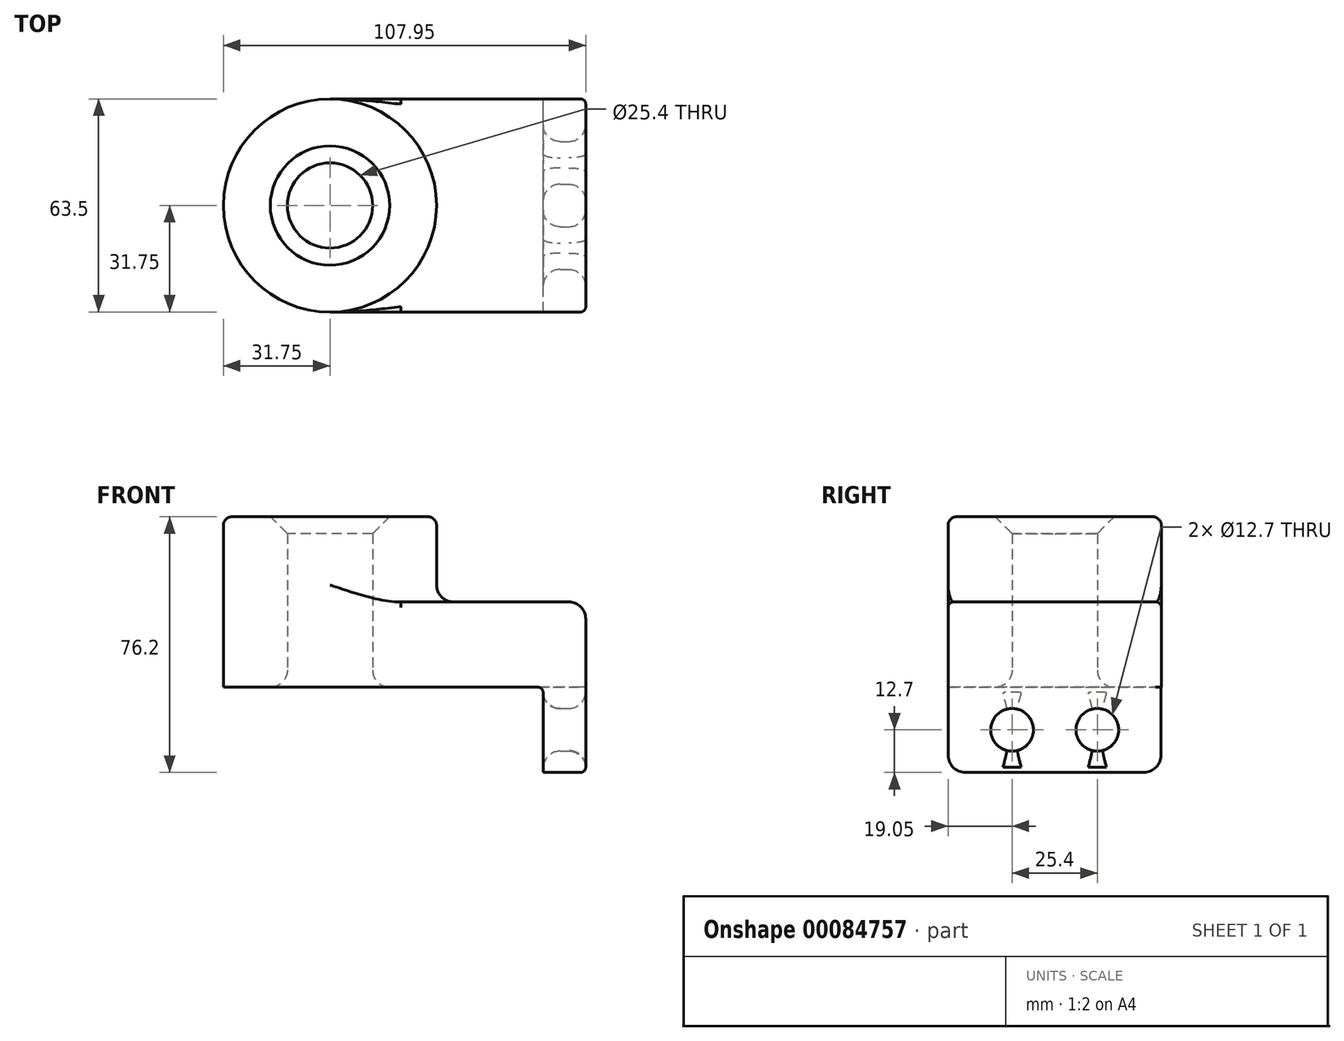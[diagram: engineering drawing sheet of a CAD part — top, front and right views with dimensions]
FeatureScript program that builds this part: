
annotation { "Feature Type Name" : "Feature", "Feature Type Description" : "" }
export const myFeature = defineFeature(function(context is Context, id is Id, definition is map)
    precondition{}
    {
        {
            var Q0;
            Q0=qCreatedBy(makeId("Top.planeOp"),FACE);
            var sketch = newSketch(context, id + "F0", { "sketchPlane" : qUnion([Q0])});
            skLineSegment(sketch, "E0.bottom", {"start": v(38.1, 31.75) * mm, "end": v(-38.1, 31.75) * mm});
            skLineSegment(sketch, "E0.top", {"start": v(38.1, -31.75) * mm, "end": v(-38.1, -31.75) * mm});
            skLineSegment(sketch, "E0.left", {"start": v(38.1, 31.75) * mm, "end": v(38.1, -31.75) * mm});
            skLineSegment(sketch, "E0.right", {"start": v(-38.1, 31.75) * mm, "end": v(-38.1, -31.75) * mm});
            skPoint(sketch, "E0.middle", {"position": v(0, 0) * mm});
            skCircle(sketch, "E1", {"center": v(-38.1, 0) * mm, "radius": 31.75 * mm});
            skCircle(sketch, "E2", {"center": v(-38.1, 0) * mm, "radius": 12.7 * mm});
            skSolve(sketch);
        }
        {
            var Q0;
            {var subQ0=sQuery(id+"F0.wireOp",EDGE,"E0.bottom");Q0=makeQuery(id+"F0.imprint","IMPRINT",FACE,{"disambiguationData":[TD([[makeQuery(id+"F0.imprint","IMPRINT",EDGE,{"derivedFrom":subQ0}),1.0]])]});}
            var Q1;
            {var subQ1=sQuery(id+"F0.wireOp",EDGE,"E0.right");var subQ3=sQuery(id+"F0.wireOp",EDGE,"E2");var subQ4=makeQuery(id+"F0.imprint","INTERSECT",VERTEX,{"disambiguationData":[OD(0.0)],"derivedFrom":[subQ1,subQ3]});Q1=makeQuery(id+"F0.imprint","IMPRINT",FACE,{"disambiguationData":[TD([[makeQuery(id+"F0.imprint","IMPRINT",EDGE,{"disambiguationData":[TD([[subQ4,1.0]])],"derivedFrom":subQ3}),-1.0]])]});}
            var Q2;
            {var subQ1=sQuery(id+"F0.wireOp",EDGE,"E0.right");var subQ3=sQuery(id+"F0.wireOp",EDGE,"E2");var subQ4=makeQuery(id+"F0.imprint","INTERSECT",VERTEX,{"disambiguationData":[OD(0.0)],"derivedFrom":[subQ1,subQ3]});Q2=makeQuery(id+"F0.imprint","IMPRINT",FACE,{"disambiguationData":[TD([[makeQuery(id+"F0.imprint","IMPRINT",EDGE,{"disambiguationData":[TD([[subQ4,-1.0]])],"derivedFrom":subQ3}),-1.0]])]});}
            extrude(context, id + "F1", {"entities" : qUnion([Q0, Q1, Q2]), "depth" : 12.7 * mm});
        }
        {
            var Q0;
            Q0 = qSketchRegion(id + "F0", true);
            extrude(context, id + "F2", {"entities" : qUnion([Q0]), "operationType" : NewBodyOperationType.ADD, "depth" : 25.4 * mm});
        }
        {
            var Q0;
            {var subQ1=sQuery(id+"F0.wireOp",EDGE,"E0.right");var subQ3=sQuery(id+"F0.wireOp",EDGE,"E2");var subQ4=makeQuery(id+"F0.imprint","INTERSECT",VERTEX,{"disambiguationData":[OD(0.0)],"derivedFrom":[subQ1,subQ3]});Q0=makeQuery(id+"F0.imprint","IMPRINT",FACE,{"disambiguationData":[TD([[makeQuery(id+"F0.imprint","IMPRINT",EDGE,{"disambiguationData":[TD([[subQ4,1.0]])],"derivedFrom":subQ3}),-1.0]])]});}
            var Q1;
            {var subQ1=sQuery(id+"F0.wireOp",EDGE,"E0.right");var subQ3=sQuery(id+"F0.wireOp",EDGE,"E2");var subQ4=makeQuery(id+"F0.imprint","INTERSECT",VERTEX,{"disambiguationData":[OD(0.0)],"derivedFrom":[subQ1,subQ3]});Q1=makeQuery(id+"F0.imprint","IMPRINT",FACE,{"disambiguationData":[TD([[makeQuery(id+"F0.imprint","IMPRINT",EDGE,{"disambiguationData":[TD([[subQ4,-1.0]])],"derivedFrom":subQ3}),-1.0]])]});}
            extrude(context, id + "F3", {"entities" : qUnion([Q0, Q1]), "operationType" : NewBodyOperationType.ADD, "depth" : 25.4 * mm});
        }
        {
            var Q0;
            {var subQ1=sQuery(id+"F0.wireOp",EDGE,"E0.right");var subQ3=sQuery(id+"F0.wireOp",EDGE,"E2");var subQ4=makeQuery(id+"F0.imprint","INTERSECT",VERTEX,{"disambiguationData":[OD(0.0)],"derivedFrom":[subQ1,subQ3]});Q0=makeQuery(id+"F0.imprint","IMPRINT",FACE,{"disambiguationData":[TD([[makeQuery(id+"F0.imprint","IMPRINT",EDGE,{"disambiguationData":[TD([[subQ4,-1.0]])],"derivedFrom":subQ3}),-1.0]])]});}
            var Q1;
            {var subQ1=sQuery(id+"F0.wireOp",EDGE,"E0.right");var subQ3=sQuery(id+"F0.wireOp",EDGE,"E2");var subQ4=makeQuery(id+"F0.imprint","INTERSECT",VERTEX,{"disambiguationData":[OD(0.0)],"derivedFrom":[subQ1,subQ3]});Q1=makeQuery(id+"F0.imprint","IMPRINT",FACE,{"disambiguationData":[TD([[makeQuery(id+"F0.imprint","IMPRINT",EDGE,{"disambiguationData":[TD([[subQ4,1.0]])],"derivedFrom":subQ3}),-1.0]])]});}
            extrude(context, id + "F4", {"entities" : qUnion([Q0, Q1]), "operationType" : NewBodyOperationType.ADD, "depth" : 50.8 * mm});
        }
        {
            var Q0;
            {var subQ0=sQuery(id+"F0.wireOp",EDGE,"E0.left");Q0=makeQuery(id+"F2.boolean.opBoolean","MERGE",FACE,{"derivedFrom":[makeQuery(id+"F1.opExtrude","SWEPT_FACE",FACE,{"disambiguationData":[OSD([subQ0])]}),makeQuery(id+"F2.opExtrude","SWEPT_FACE",FACE,{"disambiguationData":[OSD([subQ0])]})]});}
            var sketch = newSketch(context, id + "F5", { "sketchPlane" : qUnion([Q0])});
            skLineSegment(sketch, "E3.bottom", {"start": v(-31.75, 25.4) * mm, "end": v(31.64, 25.4) * mm});
            skLineSegment(sketch, "E3.top", {"start": v(-31.75, -25.4) * mm, "end": v(31.64, -25.4) * mm});
            skLineSegment(sketch, "E3.left", {"start": v(-31.75, 25.4) * mm, "end": v(-31.75, -25.4) * mm});
            skLineSegment(sketch, "E3.right", {"start": v(31.64, 25.4) * mm, "end": v(31.64, -25.4) * mm});
            skLineSegment(sketch, "E4", {"start": v(0, 0) * mm, "end": v(0, -25.4) * mm, "construction": true});
            skCircle(sketch, "E5", {"center": v(-12.7, -12.7) * mm, "radius": 6.35 * mm});
            skCircle(sketch, "E6.MirrorC", {"center": v(12.7, -12.7) * mm, "radius": 6.35 * mm});
            skSolve(sketch);
        }
        {
            var Q0;
            {var subQ7=sQuery(id+"F5.wireOp",EDGE,"E3.bottom");Q0=makeQuery(id+"F5.imprint","IMPRINT",FACE,{"disambiguationData":[TD([[makeQuery(id+"F5.imprint","IMPRINT",EDGE,{"derivedFrom":subQ7}),1.0]])]});}
            var Q1;
            {var subQ8=sQuery(id+"F5.wireOp",EDGE,"E3.top");Q1=makeQuery(id+"F5.imprint","IMPRINT",FACE,{"disambiguationData":[TD([[makeQuery(id+"F5.imprint","IMPRINT",EDGE,{"derivedFrom":subQ8}),1.0]])]});}
            extrude(context, id + "F6", {"entities" : qUnion([Q0, Q1]), "operationType" : NewBodyOperationType.ADD, "oppositeDirection" : true, "depth" : 12.7 * mm});
        }
        {
            var Q0;
            {var subQ0=sQuery(id+"F0.wireOp",EDGE,"E1");Q0=makeQuery(id+"F4.boolean.opBoolean","INTERSECT",EDGE,{"derivedFrom":[makeQuery(id+"F2.opExtrude","CAP_FACE",FACE,{"disambiguationData":[OSD([sQuery(id+"F0.wireOp",EDGE,"E0.bottom"),sQuery(id+"F0.wireOp",EDGE,"E0.top"),sQuery(id+"F0.wireOp",EDGE,"E0.left"),subQ0,sQuery(id+"F0.wireOp",EDGE,"E2")])],"isStart":false}),makeQuery(id+"F4.opExtrude","SWEPT_FACE",FACE,{"disambiguationData":[OSD([subQ0])]})]});}
            fillet(context, id + "F7", {"entities" : qUnion([Q0]), "radius" : 5.08 * mm, "tangentPropagation" : true, "allowEdgeOverflow" : false});
        }
        {
            var Q0;
            Q0=makeQuery(id+"F2.opExtrude","CAP_EDGE",EDGE,{"disambiguationData":[OSD([sQuery(id+"F0.wireOp",EDGE,"E0.left")])],"isStart":false});
            var Q1;
            Q1=makeQuery(id+"F6.opExtrude","SWEPT_EDGE",EDGE,{"disambiguationData":[OSD([sQuery(id+"F5.wireOp",EDGE,"E3.top"),sQuery(id+"F5.wireOp",EDGE,"E3.left")])]});
            var Q2;
            Q2=makeQuery(id+"F6.opExtrude","SWEPT_EDGE",EDGE,{"disambiguationData":[OSD([sQuery(id+"F5.wireOp",EDGE,"E3.top"),sQuery(id+"F5.wireOp",EDGE,"E3.right")])]});
            fillet(context, id + "F8", {"entities" : qUnion([Q0, Q1, Q2]), "radius" : 5.08 * mm, "tangentPropagation" : true, "allowEdgeOverflow" : false});
        }
        {
            var Q0;
            Q0=makeQuery(id+"F2.opExtrude","CAP_EDGE",EDGE,{"disambiguationData":[OSD([sQuery(id+"F0.wireOp",EDGE,"E0.top")])],"isStart":false});
            fillet(context, id + "F9", {"entities" : qUnion([Q0]), "radius" : 1.59 * mm, "tangentPropagation" : true, "allowEdgeOverflow" : false});
        }
        {
            var Q0;
            Q0=makeQuery(id+"F2.opExtrude","CAP_EDGE",EDGE,{"disambiguationData":[OSD([sQuery(id+"F0.wireOp",EDGE,"E0.bottom")])],"isStart":false});
            fillet(context, id + "F10", {"entities" : qUnion([Q0]), "radius" : 1.59 * mm, "tangentPropagation" : true, "allowEdgeOverflow" : false});
        }
        {
            var Q0;
            Q0=makeQuery(id+"F6.boolean.opBoolean","INTERSECT",EDGE,{"derivedFrom":[makeQuery(id+"F1.opExtrude","CAP_FACE",FACE,{"disambiguationData":[OSD([sQuery(id+"F0.wireOp",EDGE,"E0.bottom"),sQuery(id+"F0.wireOp",EDGE,"E0.top"),sQuery(id+"F0.wireOp",EDGE,"E0.left"),sQuery(id+"F0.wireOp",EDGE,"E1"),sQuery(id+"F0.wireOp",EDGE,"E2")])],"isStart":true}),makeQuery(id+"F6.opExtrude","CAP_FACE",FACE,{"disambiguationData":[OSD([sQuery(id+"F5.wireOp",EDGE,"E3.bottom"),sQuery(id+"F5.wireOp",EDGE,"E3.top"),sQuery(id+"F5.wireOp",EDGE,"E3.left"),sQuery(id+"F5.wireOp",EDGE,"E3.right"),sQuery(id+"F5.wireOp",EDGE,"E5"),sQuery(id+"F5.wireOp",EDGE,"E6.MirrorC")])],"isStart":false})]});
            fillet(context, id + "F11", {"entities" : qUnion([Q0]), "radius" : 1.59 * mm, "tangentPropagation" : true, "allowEdgeOverflow" : false});
        }
        {
            var Q0;
            Q0=makeQuery(id+"F4.opExtrude","CAP_EDGE",EDGE,{"disambiguationData":[OSD([sQuery(id+"F0.wireOp",EDGE,"E2")])],"isStart":false});
            chamfer(context, id + "F12", {"entities" : qUnion([Q0]), "width" : 5.08 * mm, "tangentPropagation" : true});
        }
        {
            var Q0;
            Q0=makeQuery(id+"F4.opExtrude","CAP_EDGE",EDGE,{"disambiguationData":[OSD([sQuery(id+"F0.wireOp",EDGE,"E1")])],"isStart":false});
            fillet(context, id + "F13", {"entities" : qUnion([Q0]), "radius" : 2.54 * mm, "tangentPropagation" : true, "allowEdgeOverflow" : false});
        }
        {
            var Q0;
            Q0=makeQuery(id+"F6.opExtrude","CAP_EDGE",EDGE,{"disambiguationData":[OSD([sQuery(id+"F5.wireOp",EDGE,"E5")])],"isStart":true});
            var Q1;
            Q1=makeQuery(id+"F6.opExtrude","CAP_EDGE",EDGE,{"disambiguationData":[OSD([sQuery(id+"F5.wireOp",EDGE,"E6.MirrorC")])],"isStart":true});
            var Q2;
            Q2=makeQuery(id+"F6.opExtrude","CAP_EDGE",EDGE,{"disambiguationData":[OSD([sQuery(id+"F5.wireOp",EDGE,"E6.MirrorC")])],"isStart":false});
            var Q3;
            Q3=makeQuery(id+"F6.opExtrude","CAP_EDGE",EDGE,{"disambiguationData":[OSD([sQuery(id+"F5.wireOp",EDGE,"E5")])],"isStart":false});
            fillet(context, id + "F14", {"entities" : qUnion([Q0, Q1, Q2, Q3]), "radius" : 5.08 * mm, "tangentPropagation" : true, "allowEdgeOverflow" : false});
        }
        {
            var Q0;
            Q0=makeQuery(id+"F1.opExtrude","CAP_EDGE",EDGE,{"disambiguationData":[OSD([sQuery(id+"F0.wireOp",EDGE,"E2")])],"isStart":true});
            fillet(context, id + "F15", {"entities" : qUnion([Q0]), "radius" : 5.08 * mm, "tangentPropagation" : true, "allowEdgeOverflow" : false});
        }
    });
